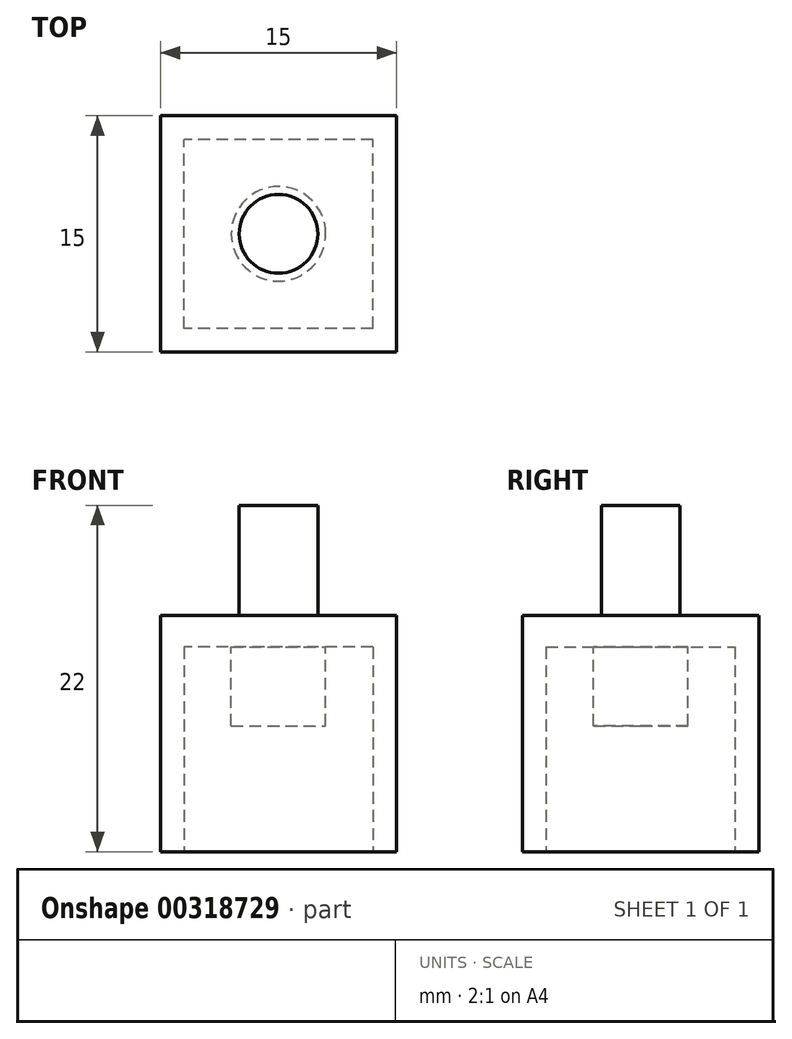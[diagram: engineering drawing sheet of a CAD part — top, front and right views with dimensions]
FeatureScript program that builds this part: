
annotation { "Feature Type Name" : "Feature", "Feature Type Description" : "" }
export const myFeature = defineFeature(function(context is Context, id is Id, definition is map)
    precondition{}
    {
        {
            var Q0;
            Q0=qCreatedBy(makeId("Top.planeOp"),FACE);
            var sketch = newSketch(context, id + "F0", { "sketchPlane" : qUnion([Q0])});
            skLineSegment(sketch, "E0.bottom", {"start": v(7.5, 7.5) * mm, "end": v(-7.5, 7.5) * mm});
            skLineSegment(sketch, "E0.top", {"start": v(7.5, -7.5) * mm, "end": v(-7.5, -7.5) * mm});
            skLineSegment(sketch, "E0.left", {"start": v(7.5, 7.5) * mm, "end": v(7.5, -7.5) * mm});
            skLineSegment(sketch, "E0.right", {"start": v(-7.5, 7.5) * mm, "end": v(-7.5, -7.5) * mm});
            skPoint(sketch, "E0.middle", {"position": v(0, 0) * mm});
            skSolve(sketch);
        }
        {
            var Q0;
            Q0 = qSketchRegion(id + "F0", true);
            extrude(context, id + "F1", {"entities" : qUnion([Q0]), "depth" : 15 * mm, "offsetDistance" : 25 * mm});
        }
        {
            var Q0;
            Q0=makeQuery(id+"F1.opExtrude","CAP_FACE",FACE,{"disambiguationData":[OSD([sQuery(id+"F0.wireOp",EDGE,"E0.bottom"),sQuery(id+"F0.wireOp",EDGE,"E0.top"),sQuery(id+"F0.wireOp",EDGE,"E0.left"),sQuery(id+"F0.wireOp",EDGE,"E0.right")])],"isStart":false});
            var sketch = newSketch(context, id + "F2", { "sketchPlane" : qUnion([Q0])});
            skPoint(sketch, "E1.0", {"position": v(0, 0) * mm});
            skCircle(sketch, "E2", {"center": v(0, 0) * mm, "radius": 2.5 * mm});
            skSolve(sketch);
        }
        {
            var Q0;
            Q0 = qSketchRegion(id + "F2", true);
            extrude(context, id + "F3", {"entities" : qUnion([Q0]), "operationType" : NewBodyOperationType.ADD, "depth" : 7 * mm, "offsetDistance" : 25 * mm});
        }
        {
            var Q0;
            Q0=makeQuery(id+"F1.opExtrude","CAP_FACE",FACE,{"disambiguationData":[OSD([sQuery(id+"F0.wireOp",EDGE,"E0.bottom"),sQuery(id+"F0.wireOp",EDGE,"E0.top"),sQuery(id+"F0.wireOp",EDGE,"E0.left"),sQuery(id+"F0.wireOp",EDGE,"E0.right")])],"isStart":true});
            var sketch = newSketch(context, id + "F4", { "sketchPlane" : qUnion([Q0])});
            skLineSegment(sketch, "E3.bottom", {"start": v(6, 6) * mm, "end": v(-6, 6) * mm});
            skLineSegment(sketch, "E3.top", {"start": v(6, -6) * mm, "end": v(-6, -6) * mm});
            skLineSegment(sketch, "E3.left", {"start": v(6, 6) * mm, "end": v(6, -6) * mm});
            skLineSegment(sketch, "E3.right", {"start": v(-6, 6) * mm, "end": v(-6, -6) * mm});
            skPoint(sketch, "E3.middle", {"position": v(0, 0) * mm});
            skSolve(sketch);
        }
        {
            var Q0;
            Q0 = qSketchRegion(id + "F4", true);
            extrude(context, id + "F5", {"entities" : qUnion([Q0]), "operationType" : NewBodyOperationType.REMOVE, "oppositeDirection" : true, "depth" : 13 * mm, "offsetDistance" : 25 * mm});
        }
        {
            var Q0;
            Q0=makeQuery(id+"F5.boolean.opBoolean","COPY",FACE,{"derivedFrom":makeQuery(id+"F5.opExtrude","CAP_FACE",FACE,{"disambiguationData":[OSD([sQuery(id+"F4.wireOp",EDGE,"E3.bottom"),sQuery(id+"F4.wireOp",EDGE,"E3.top"),sQuery(id+"F4.wireOp",EDGE,"E3.left"),sQuery(id+"F4.wireOp",EDGE,"E3.right")])],"isStart":false})});
            var sketch = newSketch(context, id + "F6", { "sketchPlane" : qUnion([Q0])});
            skPoint(sketch, "E4.0", {"position": v(0, 0) * mm});
            skCircle(sketch, "E5", {"center": v(0, 0) * mm, "radius": 3 * mm});
            skSolve(sketch);
        }
        {
            var Q0;
            Q0 = qSketchRegion(id + "F6", true);
            extrude(context, id + "F7", {"entities" : qUnion([Q0]), "operationType" : NewBodyOperationType.ADD, "depth" : 5 * mm, "offsetDistance" : 25 * mm});
        }
    });
